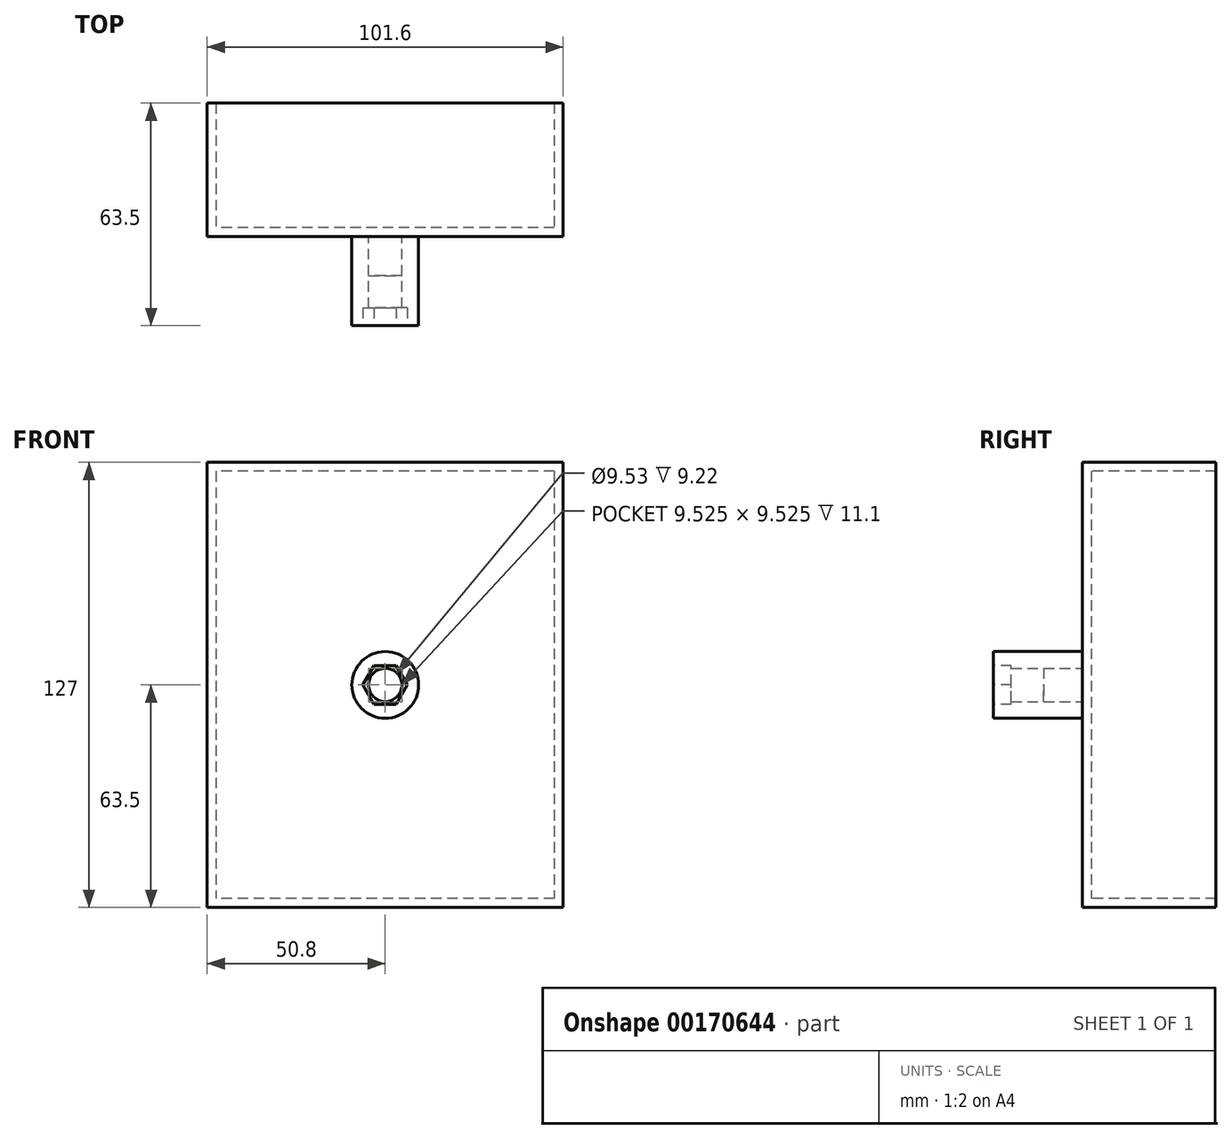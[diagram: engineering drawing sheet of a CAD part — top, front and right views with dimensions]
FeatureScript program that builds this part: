
annotation { "Feature Type Name" : "Feature", "Feature Type Description" : "" }
export const myFeature = defineFeature(function(context is Context, id is Id, definition is map)
    precondition{}
    {
        {
            var Q0;
            Q0=qCreatedBy(makeId("Front.planeOp"),FACE);
            var sketch = newSketch(context, id + "F0", { "sketchPlane" : qUnion([Q0])});
            skCircle(sketch, "E0", {"center": v(0, 0) * mm, "radius": 9.53 * mm});
            skSolve(sketch);
        }
        {
            var Q0;
            Q0 = qSketchRegion(id + "F0", true);
            extrude(context, id + "F1", {"entities" : qUnion([Q0]), "depth" : 25.4 * mm});
        }
        {
            var Q0;
            Q0=makeQuery(id+"F1.opExtrude","CAP_FACE",FACE,{"disambiguationData":[OSD([sQuery(id+"F0.wireOp",EDGE,"E0")])],"isStart":true});
            var sketch = newSketch(context, id + "F2", { "sketchPlane" : qUnion([Q0])});
            skLineSegment(sketch, "E1.bottom", {"start": v(4.76, 4.76) * mm, "end": v(-4.76, 4.76) * mm});
            skLineSegment(sketch, "E1.top", {"start": v(4.76, -4.76) * mm, "end": v(-4.76, -4.76) * mm});
            skLineSegment(sketch, "E1.left", {"start": v(4.76, 4.76) * mm, "end": v(4.76, -4.76) * mm});
            skLineSegment(sketch, "E1.right", {"start": v(-4.76, 4.76) * mm, "end": v(-4.76, -4.76) * mm});
            skPoint(sketch, "E1.middle", {"position": v(0, 0) * mm});
            skCircle(sketch, "E2", {"center": v(0, 0) * mm, "radius": 4.76 * mm});
            skSolve(sketch);
        }
        {
            var Q0;
            {var subQ0=sQuery(id+"F2.wireOp",EDGE,"E2");var subQ1=makeQuery(id+"F2.imprint","INTERSECT",VERTEX,{"derivedFrom":[sQuery(id+"F2.wireOp",EDGE,"E1.bottom"),subQ0]});Q0=makeQuery(id+"F2.imprint","IMPRINT",FACE,{"disambiguationData":[TD([[makeQuery(id+"F2.imprint","IMPRINT",EDGE,{"disambiguationData":[TD([[subQ1,1.0]])],"derivedFrom":subQ0}),1.0]])]});}
            extrude(context, id + "F3", {"entities" : qUnion([Q0]), "operationType" : NewBodyOperationType.REMOVE, "endBound" : BoundingType.THROUGH_ALL, "oppositeDirection" : true, "depth" : 25.4 * mm});
        }
        {
            var Q0;
            Q0 = qSketchRegion(id + "F2", true);
            extrude(context, id + "F4", {"entities" : qUnion([Q0]), "operationType" : NewBodyOperationType.REMOVE, "oppositeDirection" : true, "depth" : 11.1 * mm});
        }
        {
            var Q0;
            Q0=makeQuery(id+"F1.opExtrude","CAP_FACE",FACE,{"disambiguationData":[OSD([sQuery(id+"F0.wireOp",EDGE,"E0")])],"isStart":false});
            var sketch = newSketch(context, id + "F5", { "sketchPlane" : qUnion([Q0])});
            skCircle(sketch, "E3.cCircle", {"center": v(0, 0) * mm, "radius": 5.5 * mm, "construction": true});
            skLineSegment(sketch, "E3.0", {"start": v(-3.17, 5.5) * mm, "end": v(3.17, 5.5) * mm});
            skLineSegment(sketch, "E3.1", {"start": v(3.18, 5.5) * mm, "end": v(6.35, 0) * mm});
            skLineSegment(sketch, "E3.2", {"start": v(6.35, 0) * mm, "end": v(3.18, -5.5) * mm});
            skLineSegment(sketch, "E3.3", {"start": v(3.18, -5.5) * mm, "end": v(-3.17, -5.5) * mm});
            skLineSegment(sketch, "E3.4", {"start": v(-3.17, -5.5) * mm, "end": v(-6.35, 0) * mm});
            skLineSegment(sketch, "E3.5", {"start": v(-6.35, 0) * mm, "end": v(-3.17, 5.5) * mm});
            skPoint(sketch, "E3.0.midPoint", {"position": v(0, 5.5) * mm});
            skSolve(sketch);
        }
        {
            var Q0;
            Q0 = qSketchRegion(id + "F5", true);
            extrude(context, id + "F6", {"entities" : qUnion([Q0]), "operationType" : NewBodyOperationType.REMOVE, "oppositeDirection" : true, "depth" : 5.08 * mm});
        }
        {
            var Q0;
            Q0=qCreatedBy(makeId("Front.planeOp"),FACE);
            var sketch = newSketch(context, id + "F7", { "sketchPlane" : qUnion([Q0])});
            skLineSegment(sketch, "E4.bottom", {"start": v(50.8, 63.5) * mm, "end": v(-50.8, 63.5) * mm});
            skLineSegment(sketch, "E4.top", {"start": v(50.8, -63.5) * mm, "end": v(-50.8, -63.5) * mm});
            skLineSegment(sketch, "E4.left", {"start": v(50.8, 63.5) * mm, "end": v(50.8, -63.5) * mm});
            skLineSegment(sketch, "E4.right", {"start": v(-50.8, 63.5) * mm, "end": v(-50.8, -63.5) * mm});
            skLineSegment(sketch, "E5", {"start": v(50.8, 63.5) * mm, "end": v(-50.8, -63.5) * mm, "construction": true});
            skSolve(sketch);
        }
        {
            var Q0;
            Q0 = qSketchRegion(id + "F7", true);
            extrude(context, id + "F8", {"entities" : qUnion([Q0]), "operationType" : NewBodyOperationType.ADD, "oppositeDirection" : true, "depth" : 38.1 * mm});
        }
        {
            var Q0;
            Q0=makeQuery(id+"F8.opExtrude","CAP_FACE",FACE,{"disambiguationData":[OSD([sQuery(id+"F7.wireOp",EDGE,"E4.bottom"),sQuery(id+"F7.wireOp",EDGE,"E4.top"),sQuery(id+"F7.wireOp",EDGE,"E4.left"),sQuery(id+"F7.wireOp",EDGE,"E4.right")])],"isStart":false});
            shell(context, id + "F9", {"entities" : qUnion([Q0]), "thickness" : 2.54 * mm});
        }
    });
